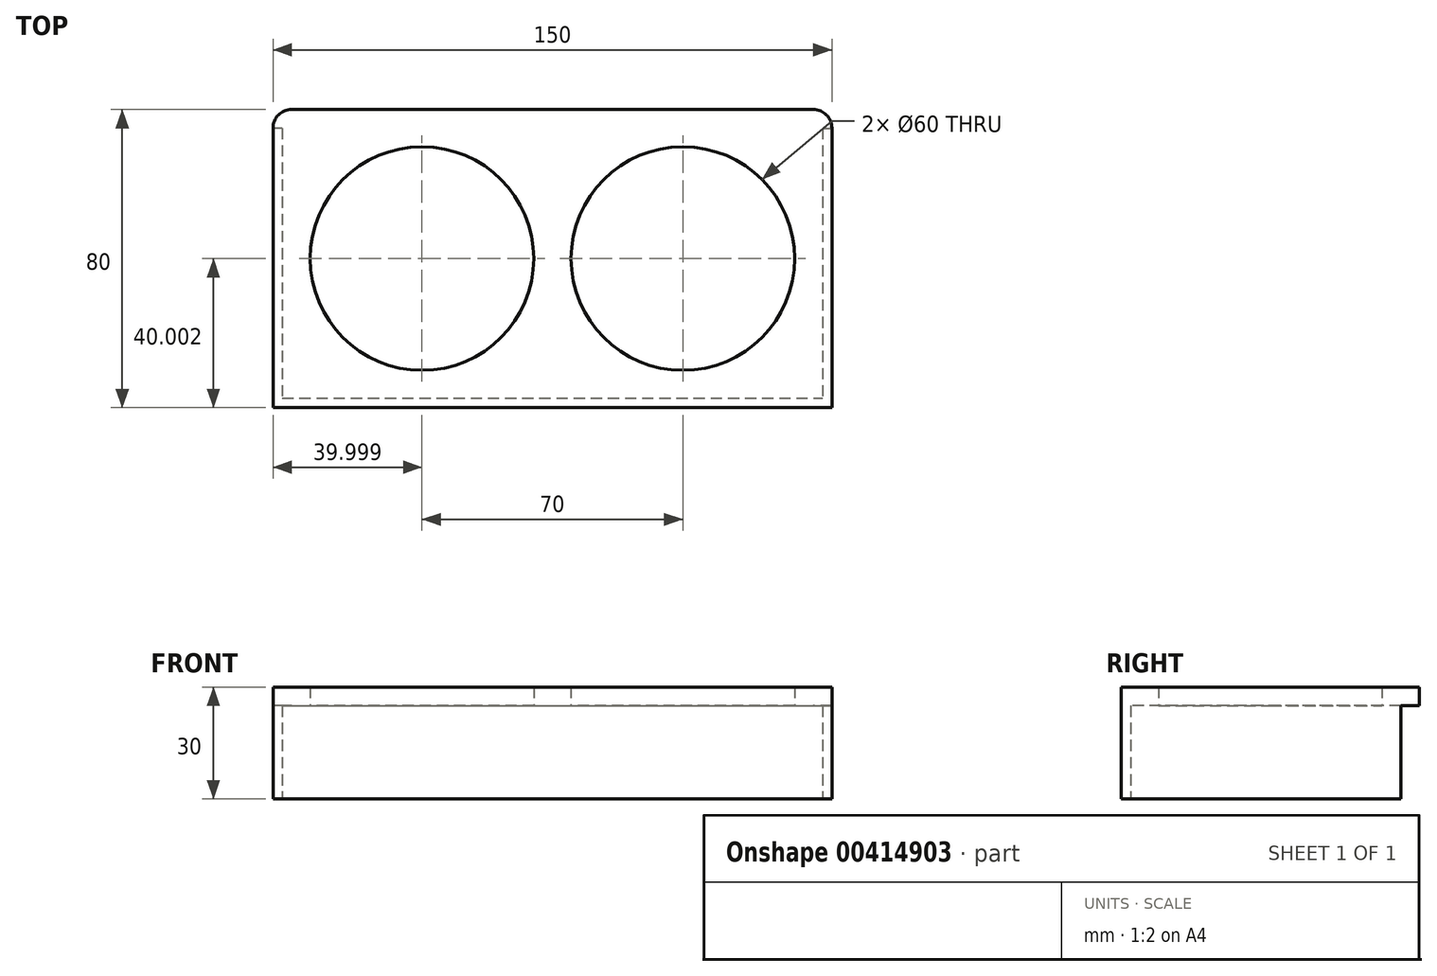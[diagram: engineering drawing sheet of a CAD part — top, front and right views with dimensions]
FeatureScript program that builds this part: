
annotation { "Feature Type Name" : "Feature", "Feature Type Description" : "" }
export const myFeature = defineFeature(function(context is Context, id is Id, definition is map)
    precondition{}
    {
        {
            var Q0;
            Q0=qCreatedBy(makeId("Top.planeOp"),FACE);
            var sketch = newSketch(context, id + "F0", { "sketchPlane" : qUnion([Q0])});
            skLineSegment(sketch, "E0.bottom", {"start": v(-85.14, 26.61) * mm, "end": v(54.86, 26.61) * mm});
            skLineSegment(sketch, "E0.top", {"start": v(-90.14, -53.39) * mm, "end": v(59.86, -53.39) * mm});
            skLineSegment(sketch, "E0.left", {"start": v(-90.14, 21.61) * mm, "end": v(-90.14, -53.39) * mm});
            skLineSegment(sketch, "E0.right", {"start": v(59.86, 21.61) * mm, "end": v(59.86, -53.39) * mm});
            skArc(sketch, "E1.filletArc", {"start": v(-85.14, 26.61) * mm, "mid": v(-88.68, 25.15) * mm, "end": v(-90.14, 21.61) * mm});
            skArc(sketch, "E2.filletArc", {"start": v(59.86, 21.61) * mm, "mid": v(58.4, 25.15) * mm, "end": v(54.86, 26.61) * mm});
            skCircle(sketch, "E3", {"center": v(-50.14, -13.39) * mm, "radius": 30 * mm});
            skCircle(sketch, "E4", {"center": v(19.86, -13.39) * mm, "radius": 30 * mm});
            skSolve(sketch);
        }
        {
            var Q0;
            Q0=sQuery(id+"F0.wireOp",EDGE,"E0.top");
            extrude(context, id + "F1", {"bodyType" : ToolBodyType.SURFACE, "surfaceEntities" : qUnion([Q0]), "oppositeDirection" : true, "depth" : 25 * mm});
        }
        {
            var Q0;
            Q0=makeQuery(id+"F0.imprint","IMPRINT",FACE,{"disambiguationData":[TD([[makeQuery(id+"F0.imprint","IMPRINT",EDGE,{"derivedFrom":sQuery(id+"F0.wireOp",EDGE,"E0.bottom")}),-1.0]])]});
            extrude(context, id + "F2", {"entities" : qUnion([Q0]), "depth" : 5 * mm});
        }
        {
            var Q0;
            Q0=makeQuery(id+"F1.opExtrude","SWEPT_FACE",FACE,{"disambiguationData":[OSD([sQuery(id+"F0.wireOp",EDGE,"E0.top")])]});
            extrude(context, id + "F3", {"entities" : qUnion([Q0]), "operationType" : NewBodyOperationType.ADD, "depth" : 2.5 * mm});
        }
        {
            var Q0;
            Q0=sQuery(id+"F0.wireOp",EDGE,"E0.left");
            extrude(context, id + "F4", {"bodyType" : ToolBodyType.SURFACE, "surfaceEntities" : qUnion([Q0]), "oppositeDirection" : true, "depth" : 25 * mm});
        }
        {
            var Q0;
            Q0=sQuery(id+"F0.wireOp",EDGE,"E0.right");
            extrude(context, id + "F5", {"bodyType" : ToolBodyType.SURFACE, "surfaceEntities" : qUnion([Q0]), "oppositeDirection" : true, "depth" : 25 * mm});
        }
        {
            var Q0;
            Q0=makeQuery(id+"F5.opExtrude","SWEPT_FACE",FACE,{"disambiguationData":[OSD([sQuery(id+"F0.wireOp",EDGE,"E0.right")])]});
            extrude(context, id + "F6", {"entities" : qUnion([Q0]), "operationType" : NewBodyOperationType.ADD, "oppositeDirection" : true, "depth" : 2.5 * mm});
        }
        {
            var Q0;
            Q0=makeQuery(id+"F4.opExtrude","SWEPT_FACE",FACE,{"disambiguationData":[OSD([sQuery(id+"F0.wireOp",EDGE,"E0.left")])]});
            extrude(context, id + "F7", {"entities" : qUnion([Q0]), "operationType" : NewBodyOperationType.ADD, "depth" : 2.5 * mm});
        }
    });
